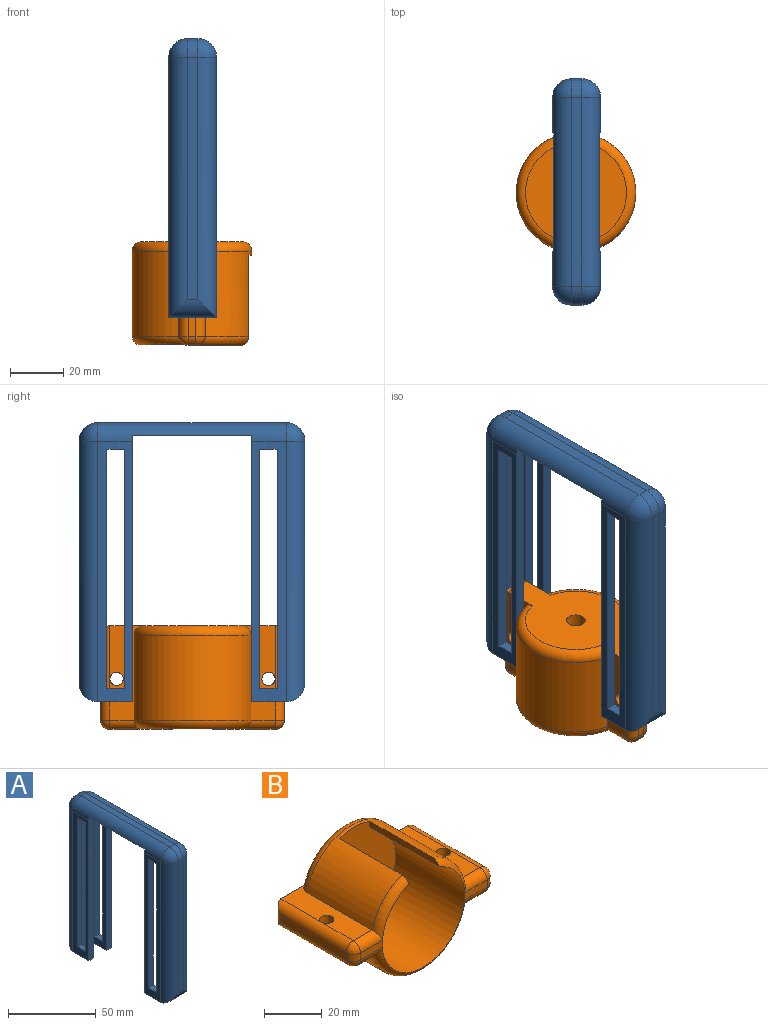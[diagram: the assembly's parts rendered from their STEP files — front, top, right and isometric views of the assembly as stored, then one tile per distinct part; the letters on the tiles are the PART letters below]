
ASSEMBLY  parts=2 mates=1
PART A: 52 faces, bbox 18x85x105 mm
  f0: plane 13x3.75mm, normal (0,0,-1), area 48.7mm2, adj f5,f7,f11,f39
  f1: plane 98x13mm, normal (-1,0,0), area 689mm2, adj f2,f25,f34,f35,f36,f37,f43,f48
  f2: plane 13x3.75mm, normal (0,0,-1), area 48.8mm2, adj f1,f23,f25,f50
  f3: plane 98x13mm, normal (1,0,0), area 689mm2, adj f26,f28,f30,f31,f32,f33,f46,f51
  f4: plane 98x13mm, normal (-1,0,0), area 689mm2, adj f8,f9,f17,f18,f19,f20,f38,f43
  f5: plane 98x13mm, normal (1,0,0), area 689mm2, adj f0,f11,f13,f14,f15,f16,f41,f46
  f6: plane 100x13mm, normal (1,0,0), area 715mm2, adj f8,f9,f12,f17,f18,f19,f20,f22
  f7: plane 100x13mm, normal (-1,0,0), area 715mm2, adj f0,f11,f12,f13,f14,f15,f16,f22
  f8: plane 100x3.75mm, normal (0,1,0), area 374.8mm2, adj f4,f6,f9,f22,f43
  f9: plane 13x3.75mm, normal (0,0,-1), area 48.7mm2, adj f4,f6,f8,f39
  f10: plane 91x4mm, normal (0,-1,0), area 364mm2, adj f38,f39,f41,f42
  f11: plane 100x3.75mm, normal (0,1,0), area 374.8mm2, adj f0,f5,f7,f22,f46
  f12: plane 100x10.5mm, normal (0,1,0), area 1050mm2, adj f6,f7,f22,f39
  f13: plane 90x3.75mm, normal (0,1,0), area 337.5mm2, adj f5,f7,f14,f16
  f14: plane 6.5x3.75mm, normal (0,0,1), area 24.4mm2, adj f5,f7,f13,f15
  f15: plane 90x3.75mm, normal (0,-1,0), area 337.5mm2, adj f5,f7,f14,f16
  f16: plane 6.5x3.75mm, normal (0,0,-1), area 24.4mm2, adj f5,f7,f13,f15
  f17: plane 6.5x3.75mm, normal (0,0,-1), area 24.4mm2, adj f4,f6,f18,f20
  f18: plane 90x3.75mm, normal (0,-1,0), area 337.5mm2, adj f4,f6,f17,f19
  f19: plane 6.5x3.75mm, normal (0,0,1), area 24.4mm2, adj f4,f6,f18,f20
  f20: plane 90x3.75mm, normal (0,1,0), area 337.5mm2, adj f4,f6,f17,f19
  f21: plane 71x4mm, normal (0,0,1), area 284mm2, adj f42,f43,f46,f47
  f22: plane 71x17.42mm, normal (0,0,-1), area 1056.7mm2, adj f6,f7,f8,f11,f12,f23,f24,f25
  f23: plane 100x13mm, normal (1,0,0), area 715mm2, adj f2,f22,f25,f29,f34,f35,f36,f37
  f24: plane 100x13mm, normal (-1,0,0), area 715mm2, adj f22,f26,f28,f29,f30,f31,f32,f33
  f25: plane 100x3.75mm, normal (0,-1,0), area 374.8mm2, adj f1,f2,f22,f23,f43
  f26: plane 13x3.75mm, normal (0,0,-1), area 48.8mm2, adj f3,f24,f28,f50
  f27: plane 91x4mm, normal (0,1,0), area 364mm2, adj f47,f48,f50,f51
  f28: plane 100x3.75mm, normal (0,-1,0), area 374.8mm2, adj f3,f22,f24,f26,f46
  f29: plane 100x10.5mm, normal (0,-1,0), area 1050mm2, adj f22,f23,f24,f50
  f30: plane 90x3.75mm, normal (0,-1,0), area 337.5mm2, adj f3,f24,f31,f33
  f31: plane 6.5x3.75mm, normal (0,0,1), area 24.4mm2, adj f3,f24,f30,f32
  f32: plane 90x3.75mm, normal (0,1,0), area 337.5mm2, adj f3,f24,f31,f33
  f33: plane 6.5x3.75mm, normal (0,0,-1), area 24.4mm2, adj f3,f24,f30,f32
  f34: plane 6.5x3.75mm, normal (0,0,-1), area 24.4mm2, adj f1,f23,f35,f37
  f35: plane 90x3.75mm, normal (0,1,0), area 337.5mm2, adj f1,f23,f34,f36
  f36: plane 6.5x3.75mm, normal (0,0,1), area 24.4mm2, adj f1,f23,f35,f37
  f37: plane 90x3.75mm, normal (0,-1,0), area 337.5mm2, adj f1,f23,f34,f36
  f38: cylinder r=7mm len=98mm, axis (0,0,1), area 1049.6mm2, adj f4,f10,f39,f40
  f39: cylinder r=7mm len=18mm, axis (-1,0,0), area 142mm2, adj f0,f9,f10,f12,f38,f41
  f40: sphere r=7mm, area 77mm2, adj f38,f42,f43
  f41: cylinder r=7mm len=98mm, axis (0,0,-1), area 1049.6mm2, adj f5,f10,f39,f44
  f42: cylinder r=7mm len=7mm, axis (1,0,0), area 44mm2, adj f10,f21,f40,f44
  f43: cylinder r=7mm len=71mm, axis (0,-1,0), area 689.4mm2, adj f1,f4,f8,f21,f22,f25,f40,f45
  f44: sphere r=7mm, area 77mm2, adj f41,f42,f46
  f45: sphere r=7mm, area 77mm2, adj f43,f47,f48
  f46: cylinder r=7mm len=71mm, axis (0,1,0), area 689.4mm2, adj f3,f5,f11,f21,f22,f28,f44,f49
  f47: cylinder r=7mm len=7mm, axis (1,0,0), area 44mm2, adj f21,f27,f45,f49
  f48: cylinder r=7mm len=98mm, axis (0,0,1), area 1049.6mm2, adj f1,f27,f45,f50
  f49: sphere r=7mm, area 77mm2, adj f46,f47,f51
  f50: cylinder r=7mm len=18mm, axis (-1,0,0), area 142mm2, adj f2,f26,f27,f29,f48,f51
  f51: cylinder r=7mm len=98mm, axis (0,0,-1), area 1049.6mm2, adj f3,f27,f49,f50
PART B: 39 faces, bbox 69.2x39.2x48.7 mm
  f0: plane 10.91x3mm, normal (0,-1,0), area 32.6mm2, adj f2,f21,f29,f34
  f1: cylinder r=22.5mm len=43.88mm, axis (0,1,0), area 1939.3mm2, adj f11,f14,f36,f37
  f2: cylinder r=20.25mm len=40.5mm, axis (0,1,0), area 3792.4mm2, adj f0,f4,f5,f8,f9,f18,f19,f34
  f3: cylinder r=22.5mm len=43.88mm, axis (0,1,0), area 1485.5mm2, adj f5,f8,f9,f10,f13,f18,f19,f21
  f4: plane 10.91x3mm, normal (0,-1,0), area 32.6mm2, adj f2,f22,f30,f35
  f5: plane 42.75x40.5mm, normal (0,-1,0), area 1284.1mm2, adj f2,f3,f7,f8,f9
  f6: plane 62.21x38mm, normal (0,1,0), area 1342.1mm2, adj f7,f10,f11,f13,f14,f24,f27,f37
  f7: cylinder r=3.5mm len=7mm, axis (0,1,0), area 110mm2, adj f5,f6
  f8: plane 34x2.4mm, normal (1,0,0), area 79.4mm2, adj f2,f3,f5,f18
  f9: plane 34x2.41mm, normal (-1,0,0), area 79.7mm2, adj f2,f3,f5,f19
  f10: plane 35.5x12.77mm, normal (0,0,1), area 308.5mm2, adj f3,f6,f17,f22,f23,f38
  f11: plane 35.5x12.77mm, normal (0,0,-1), area 308.5mm2, adj f1,f6,f17,f31,f35,f37
  f12: plane 32x3mm, normal (1,0,0), area 96mm2, adj f23,f27,f30,f31
  f13: plane 35.5x12.77mm, normal (0,0,1), area 308.5mm2, adj f3,f6,f16,f20,f21,f38
  f14: plane 35.5x12.77mm, normal (0,0,-1), area 308.5mm2, adj f1,f6,f16,f28,f34,f37
  f15: plane 32x3mm, normal (-1,0,0), area 96mm2, adj f20,f24,f28,f29
  f16: cylinder r=2.5mm len=10mm, axis (0,0,1), area 157.1mm2, adj f13,f14
  f17: cylinder r=2.5mm len=10mm, axis (0,0,1), area 157.1mm2, adj f10,f11
  f18: torus R=19mm, axis (0,-1,0), area 95.3mm2, adj f2,f3,f8,f21
  f19: torus R=19mm, axis (0,-1,0), area 94.4mm2, adj f2,f3,f9,f22
  f20: cylinder r=3.5mm len=35.5mm, axis (0,1,0), area 188.2mm2, adj f13,f15,f24,f25
  f21: cylinder r=3.5mm len=10.91mm, axis (-1,0,0), area 54.5mm2, adj f0,f3,f13,f18,f25
  f22: cylinder r=3.5mm len=10.91mm, axis (1,0,0), area 54.5mm2, adj f3,f4,f10,f19,f26
  f23: cylinder r=3.5mm len=35.5mm, axis (0,-1,0), area 188.2mm2, adj f10,f12,f26,f27
  f24: cylinder r=3.5mm len=10mm, axis (0,0,1), area 41mm2, adj f6,f15,f20,f28
  f25: sphere r=3.5mm, area 19.2mm2, adj f20,f21,f29
  f26: sphere r=3.5mm, area 19.2mm2, adj f22,f23,f30
  f27: cylinder r=3.5mm len=10mm, axis (0,0,-1), area 41mm2, adj f6,f12,f23,f31
  f28: cylinder r=3.5mm len=35.5mm, axis (0,-1,0), area 188.2mm2, adj f14,f15,f24,f32
  f29: cylinder r=3.5mm len=3.5mm, axis (0,0,1), area 16.5mm2, adj f0,f15,f25,f32
  f30: cylinder r=3.5mm len=3.5mm, axis (0,0,-1), area 16.5mm2, adj f4,f12,f26,f33
  f31: cylinder r=3.5mm len=35.5mm, axis (0,1,0), area 188.2mm2, adj f11,f12,f27,f33
  f32: sphere r=3.5mm, area 19.2mm2, adj f28,f29,f34
  f33: sphere r=3.5mm, area 19.2mm2, adj f30,f31,f35
  f34: cylinder r=3.5mm len=11.04mm, axis (1,0,0), area 55.4mm2, adj f0,f2,f14,f32,f36
  f35: cylinder r=3.5mm len=11.04mm, axis (-1,0,0), area 55.4mm2, adj f2,f4,f11,f33,f36
  f36: torus R=19mm, axis (0,-1,0), area 252mm2, adj f1,f2,f34,f35
  f37: torus R=19mm, axis (0,1,0), area 311.1mm2, adj f1,f6,f11,f14
  f38: torus R=19mm, axis (0,1,0), area 311.1mm2, adj f3,f6,f10,f13
PLACE A t=(28.12,20.89,-1.95)mm
PLACE B rot(axis=(0.58,0.58,0.58),120deg) t=(27.87,43.2,-28.37)mm
MATE planar B.f14 <-> A.f6  axis (-1,0,0) through (22.87,16.86,-40.83)mm
